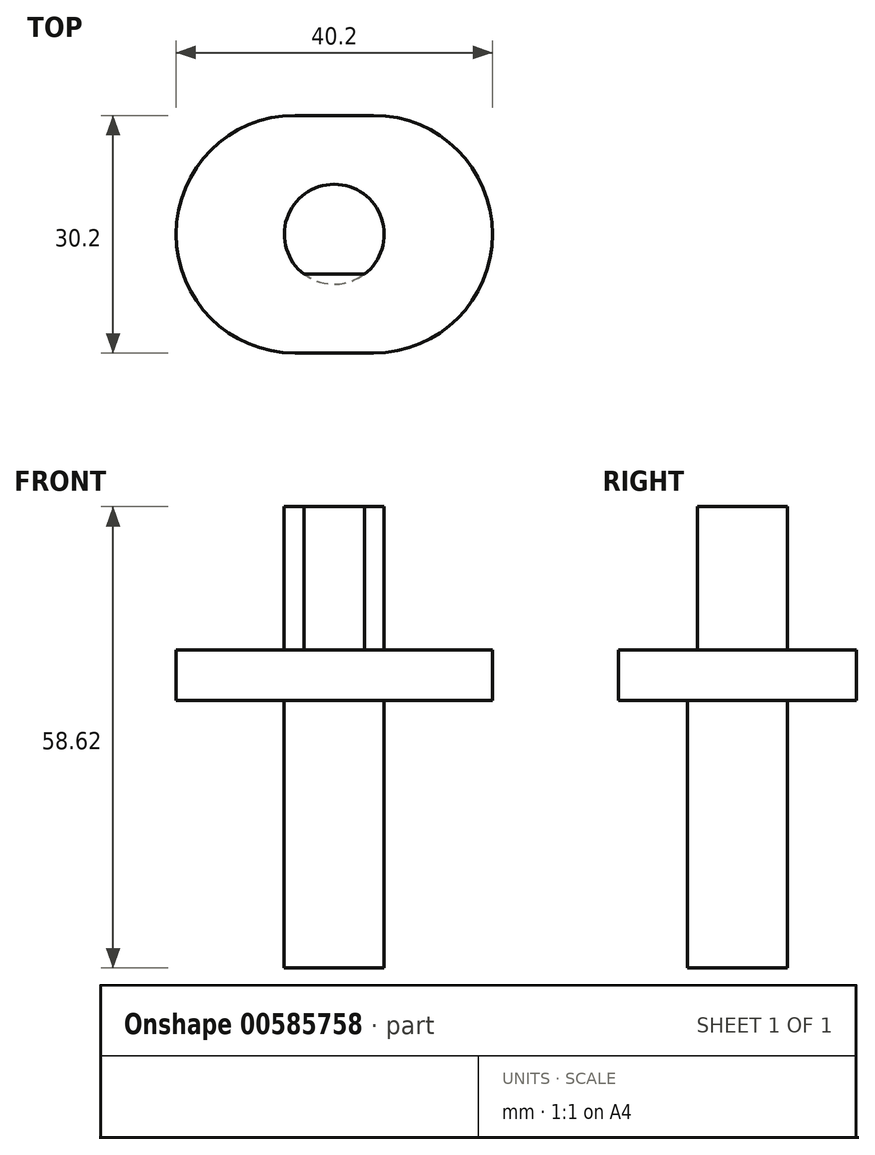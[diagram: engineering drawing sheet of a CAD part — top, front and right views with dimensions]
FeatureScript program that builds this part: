
annotation { "Feature Type Name" : "Feature", "Feature Type Description" : "" }
export const myFeature = defineFeature(function(context is Context, id is Id, definition is map)
    precondition{}
    {
        {
            var Q0;
            Q0=qCreatedBy(makeId("Top.planeOp"),FACE);
            var sketch = newSketch(context, id + "F0", { "sketchPlane" : qUnion([Q0])});
            skArc(sketch, "E0", {"start": v(-5, 15.1) * mm, "mid": v(-20.1, 0) * mm, "end": v(-5, -15.1) * mm});
            skLineSegment(sketch, "E1", {"start": v(-5, 15.1) * mm, "end": v(5, 15.1) * mm});
            skLineSegment(sketch, "E2", {"start": v(-5, -15.1) * mm, "end": v(5, -15.1) * mm});
            skArc(sketch, "E3", {"start": v(5, -15.1) * mm, "mid": v(20.1, 0) * mm, "end": v(5, 15.1) * mm});
            skPoint(sketch, "E3.centerSnap0", {"position": v(-16.9, 0) * mm});
            skLineSegment(sketch, "E4", {"start": v(-5, 0) * mm, "end": v(-20.1, 0) * mm, "construction": true});
            skLineSegment(sketch, "E5", {"start": v(0, 0) * mm, "end": v(20.1, 0) * mm, "construction": true});
            skSolve(sketch);
        }
        {
            var Q0;
            Q0=qSketchRegion(id+"F0",true);
            extrude(context, id + "F1", {"entities" : qUnion([Q0]), "depth" : 6.42 * mm, "offsetDistance" : 25 * mm});
        }
        {
            var Q0;
            Q0=makeQuery(id+"F1.opExtrude","CAP_FACE",FACE,{"disambiguationData":[OSD([sQuery(id+"F0.wireOp",EDGE,"E0"),sQuery(id+"F0.wireOp",EDGE,"E1"),sQuery(id+"F0.wireOp",EDGE,"E2"),sQuery(id+"F0.wireOp",EDGE,"E3")])],"isStart":true});
            var sketch = newSketch(context, id + "F2", { "sketchPlane" : qUnion([Q0])});
            skCircle(sketch, "E6", {"center": v(0, 0) * mm, "radius": 6.34 * mm});
            skSolve(sketch);
        }
        {
            var Q0;
            Q0=qSketchRegion(id+"F2",true);
            extrude(context, id + "F3", {"entities" : qUnion([Q0]), "operationType" : NewBodyOperationType.ADD, "depth" : 34 * mm, "offsetDistance" : 25 * mm});
        }
        {
            var Q0;
            Q0=makeQuery(id+"F1.opExtrude","CAP_FACE",FACE,{"disambiguationData":[OSD([sQuery(id+"F0.wireOp",EDGE,"E0"),sQuery(id+"F0.wireOp",EDGE,"E1"),sQuery(id+"F0.wireOp",EDGE,"E2"),sQuery(id+"F0.wireOp",EDGE,"E3")])],"isStart":false});
            var sketch = newSketch(context, id + "F4", { "sketchPlane" : qUnion([Q0])});
            skCircle(sketch, "E7", {"center": v(0, 0) * mm, "radius": 6.34 * mm});
            skSolve(sketch);
        }
        {
            var Q0;
            Q0=makeQuery(id+"F4.imprint","IMPRINT",FACE,{"disambiguationData":[TD([[makeQuery(id+"F4.imprint","IMPRINT",EDGE,{"derivedFrom":sQuery(id+"F4.wireOp",EDGE,"E7")}),1.0]])]});
            extrude(context, id + "F5", {"entities" : qUnion([Q0]), "operationType" : NewBodyOperationType.ADD, "depth" : 18.2 * mm, "offsetDistance" : 25 * mm});
        }
        {
            var Q0;
            Q0=makeQuery(id+"F5.opExtrude","CAP_FACE",FACE,{"disambiguationData":[OSD([sQuery(id+"F4.wireOp",EDGE,"E7")])],"isStart":false});
            var sketch = newSketch(context, id + "F6", { "sketchPlane" : qUnion([Q0])});
            skLineSegment(sketch, "E8", {"start": v(0, -6.34) * mm, "end": v(0, -5.07) * mm});
            skLineSegment(sketch, "E9", {"start": v(0, -5.07) * mm, "end": v(-3.82, -5.07) * mm});
            skLineSegment(sketch, "E10", {"start": v(-3.82, -5.07) * mm, "end": v(3.82, -5.07) * mm});
            skArc(sketch, "E11", {"start": v(3.82, -5.07) * mm, "mid": v(0, -6.34) * mm, "end": v(-3.82, -5.07) * mm});
            skSolve(sketch);
        }
        {
            var Q0;
            {var subQ0=sQuery(id+"F6.wireOp",EDGE,"E8");Q0=makeQuery(id+"F6.imprint","IMPRINT",FACE,{"disambiguationData":[TD([[makeQuery(id+"F6.imprint","IMPRINT",EDGE,{"derivedFrom":subQ0}),1.0]])]});}
            var Q1;
            {var subQ0=sQuery(id+"F6.wireOp",EDGE,"E8");Q1=makeQuery(id+"F6.imprint","IMPRINT",FACE,{"disambiguationData":[TD([[makeQuery(id+"F6.imprint","IMPRINT",EDGE,{"derivedFrom":subQ0}),-1.0]])]});}
            extrude(context, id + "F7", {"entities" : qUnion([Q0, Q1]), "operationType" : NewBodyOperationType.REMOVE, "oppositeDirection" : true, "depth" : 18.2 * mm, "offsetDistance" : 25 * mm});
        }
    });
